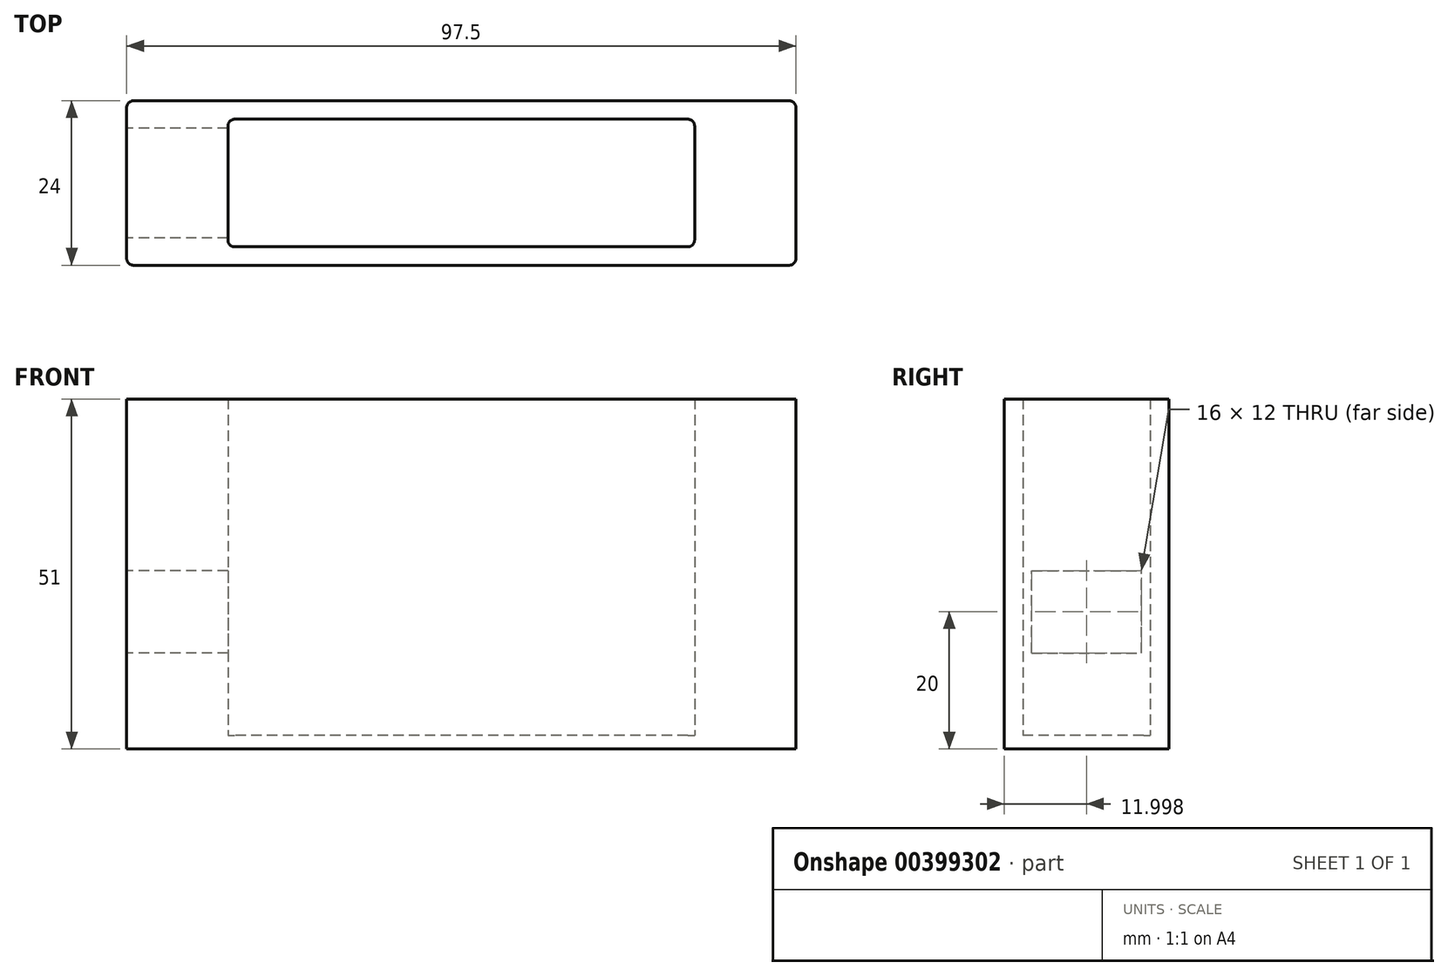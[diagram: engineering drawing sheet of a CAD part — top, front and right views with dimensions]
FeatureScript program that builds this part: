
annotation { "Feature Type Name" : "Feature", "Feature Type Description" : "" }
export const myFeature = defineFeature(function(context is Context, id is Id, definition is map)
    precondition{}
    {
        {
            var Q0;
            Q0=qCreatedBy(makeId("Top.planeOp"),FACE);
            var sketch = newSketch(context, id + "F0", { "sketchPlane" : qUnion([Q0])});
            skLineSegment(sketch, "E0.bottom", {"start": v(-40.91, 8.35) * mm, "end": v(56.59, 8.35) * mm});
            skLineSegment(sketch, "E0.top", {"start": v(-40.91, -15.65) * mm, "end": v(56.59, -15.65) * mm});
            skLineSegment(sketch, "E0.left", {"start": v(-40.91, 8.35) * mm, "end": v(-40.91, -15.65) * mm});
            skLineSegment(sketch, "E0.right", {"start": v(56.59, 8.35) * mm, "end": v(56.59, -15.65) * mm});
            skLineSegment(sketch, "E1.bottom", {"start": v(41.84, 5.65) * mm, "end": v(-26.16, 5.65) * mm});
            skLineSegment(sketch, "E1.top", {"start": v(41.84, -12.95) * mm, "end": v(-26.16, -12.95) * mm});
            skLineSegment(sketch, "E1.left", {"start": v(41.84, 5.65) * mm, "end": v(41.84, -12.95) * mm});
            skLineSegment(sketch, "E1.right", {"start": v(-26.16, 5.65) * mm, "end": v(-26.16, -12.95) * mm});
            skSolve(sketch);
        }
        {
            var Q0;
            Q0=makeQuery(id+"F0.imprint","IMPRINT",FACE,{"disambiguationData":[TD([[makeQuery(id+"F0.imprint","IMPRINT",EDGE,{"derivedFrom":sQuery(id+"F0.wireOp",EDGE,"E0.bottom")}),-1.0]])]});
            extrude(context, id + "F1", {"entities" : qUnion([Q0]), "depth" : 51 * mm});
        }
        {
            var Q0;
            Q0=makeQuery(id+"F0.imprint","IMPRINT",FACE,{"disambiguationData":[TD([[makeQuery(id+"F0.imprint","IMPRINT",EDGE,{"derivedFrom":sQuery(id+"F0.wireOp",EDGE,"E1.bottom")}),1.0]])]});
            extrude(context, id + "F2", {"entities" : qUnion([Q0]), "operationType" : NewBodyOperationType.ADD, "depth" : 2 * mm});
        }
        {
            var Q0;
            Q0=makeQuery(id+"F1.opExtrude","SWEPT_FACE",FACE,{"disambiguationData":[OSD([sQuery(id+"F0.wireOp",EDGE,"E0.left")])]});
            var sketch = newSketch(context, id + "F3", { "sketchPlane" : qUnion([Q0])});
            skLineSegment(sketch, "E2", {"start": v(3.65, 51) * mm, "end": v(3.65, 0) * mm, "construction": true});
            skLineSegment(sketch, "E3", {"start": v(3.65, 0) * mm, "end": v(3.65, 20) * mm, "construction": true});
            skLineSegment(sketch, "E4.bottom", {"start": v(11.65, 14) * mm, "end": v(-4.35, 14) * mm});
            skLineSegment(sketch, "E4.top", {"start": v(11.65, 26) * mm, "end": v(-4.35, 26) * mm});
            skLineSegment(sketch, "E4.left", {"start": v(11.65, 14) * mm, "end": v(11.65, 26) * mm});
            skLineSegment(sketch, "E4.right", {"start": v(-4.35, 14) * mm, "end": v(-4.35, 26) * mm});
            skPoint(sketch, "E4.middle", {"position": v(3.65, 20) * mm});
            skSolve(sketch);
        }
        {
            var Q0;
            Q0=makeQuery(id+"F3.imprint","IMPRINT",FACE,{"disambiguationData":[TD([[makeQuery(id+"F3.imprint","IMPRINT",EDGE,{"derivedFrom":sQuery(id+"F3.wireOp",EDGE,"E4.bottom")}),-1.0]])]});
            extrude(context, id + "F4", {"entities" : qUnion([Q0]), "operationType" : NewBodyOperationType.REMOVE, "oppositeDirection" : true, "depth" : 25 * mm});
        }
        {
            var Q0;
            Q0=makeQuery(id+"F1.opExtrude","SWEPT_EDGE",EDGE,{"disambiguationData":[OSD([sQuery(id+"F0.wireOp",EDGE,"E0.top"),sQuery(id+"F0.wireOp",EDGE,"E0.left")])]});
            var Q1;
            Q1=makeQuery(id+"F1.opExtrude","SWEPT_EDGE",EDGE,{"disambiguationData":[OSD([sQuery(id+"F0.wireOp",EDGE,"E0.bottom"),sQuery(id+"F0.wireOp",EDGE,"E0.left")])]});
            var Q2;
            Q2=makeQuery(id+"F1.opExtrude","SWEPT_EDGE",EDGE,{"disambiguationData":[OSD([sQuery(id+"F0.wireOp",EDGE,"E0.top"),sQuery(id+"F0.wireOp",EDGE,"E0.right")])]});
            var Q3;
            Q3=makeQuery(id+"F1.opExtrude","SWEPT_EDGE",EDGE,{"disambiguationData":[OSD([sQuery(id+"F0.wireOp",EDGE,"E0.bottom"),sQuery(id+"F0.wireOp",EDGE,"E0.right")])]});
            var Q4;
            Q4=makeQuery(id+"F1.opExtrude","SWEPT_EDGE",EDGE,{"disambiguationData":[OSD([sQuery(id+"F0.wireOp",EDGE,"E1.bottom"),sQuery(id+"F0.wireOp",EDGE,"E1.left")])]});
            var Q5;
            Q5=makeQuery(id+"F1.opExtrude","SWEPT_EDGE",EDGE,{"disambiguationData":[OSD([sQuery(id+"F0.wireOp",EDGE,"E1.top"),sQuery(id+"F0.wireOp",EDGE,"E1.left")])]});
            var Q6;
            Q6=makeQuery(id+"F1.opExtrude","SWEPT_EDGE",EDGE,{"disambiguationData":[OSD([sQuery(id+"F0.wireOp",EDGE,"E1.bottom"),sQuery(id+"F0.wireOp",EDGE,"E1.right")])]});
            var Q7;
            Q7=makeQuery(id+"F1.opExtrude","SWEPT_EDGE",EDGE,{"disambiguationData":[OSD([sQuery(id+"F0.wireOp",EDGE,"E1.top"),sQuery(id+"F0.wireOp",EDGE,"E1.right")])]});
            fillet(context, id + "F5", {"entities" : qUnion([Q0, Q1, Q2, Q3, Q4, Q5, Q6, Q7]), "radius" : 1 * mm, "tangentPropagation" : true, "allowEdgeOverflow" : false});
        }
    });
